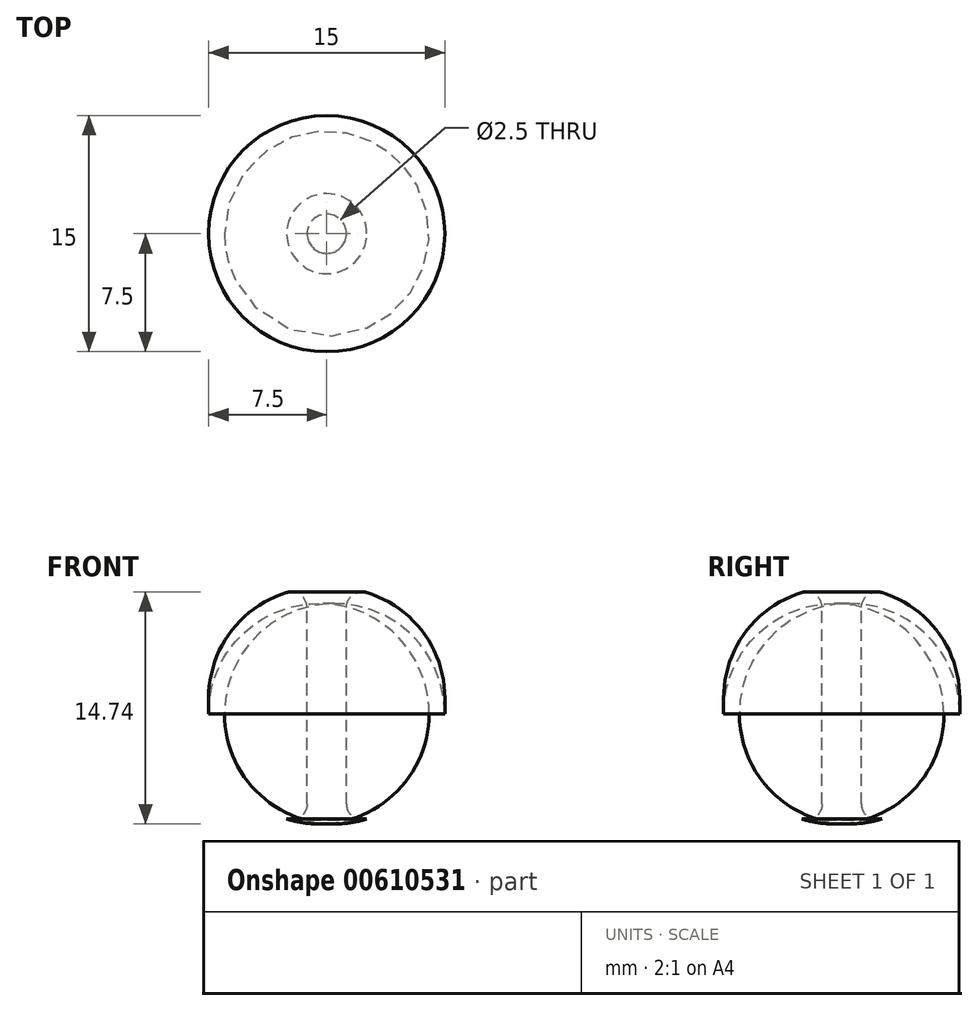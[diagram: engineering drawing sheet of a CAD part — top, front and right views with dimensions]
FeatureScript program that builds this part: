
annotation { "Feature Type Name" : "Feature", "Feature Type Description" : "" }
export const myFeature = defineFeature(function(context is Context, id is Id, definition is map)
    precondition{}
    {
        {
            var Q0;
            Q0=qCreatedBy(makeId("Top.planeOp"),FACE);
            var sketch = newSketch(context, id + "F0", { "sketchPlane" : qUnion([Q0])});
            skCircle(sketch, "E0", {"center": v(0, 0) * mm, "radius": 7.5 * mm});
            skSolve(sketch);
        }
        {
            var Q0;
            Q0=makeQuery(id+"F0.imprint","IMPRINT",FACE,{"disambiguationData":[TD([[makeQuery(id+"F0.imprint","IMPRINT",EDGE,{"derivedFrom":sQuery(id+"F0.wireOp",EDGE,"E0")}),1.0]])]});
            extrude(context, id + "F1", {"entities" : qUnion([Q0]), "depth" : 15 * mm, "offsetDistance" : 25 * mm});
        }
        {
            var Q0;
            Q0=makeQuery(id+"F1.opExtrude","CAP_EDGE",EDGE,{"disambiguationData":[OSD([sQuery(id+"F0.wireOp",EDGE,"E0")])],"isStart":false});
            fillet(context, id + "F2", {"entities" : qUnion([Q0]), "radius" : 7 * mm, "tangentPropagation" : true, "allowEdgeOverflow" : false});
        }
        {
            var Q0;
            Q0=makeQuery(id+"F1.opExtrude","CAP_EDGE",EDGE,{"disambiguationData":[OSD([sQuery(id+"F0.wireOp",EDGE,"E0")])],"isStart":true});
            fillet(context, id + "F3", {"entities" : qUnion([Q0]), "radius" : 7 * mm, "tangentPropagation" : true, "allowEdgeOverflow" : false});
        }
        {
            var Q0;
            Q0=makeQuery(id+"F1.opExtrude","CAP_FACE",FACE,{"disambiguationData":[OSD([sQuery(id+"F0.wireOp",EDGE,"E0")])],"isStart":false});
            var sketch = newSketch(context, id + "F4", { "sketchPlane" : qUnion([Q0])});
            skCircle(sketch, "E1", {"center": v(0, 0) * mm, "radius": 1.25 * mm});
            skSolve(sketch);
        }
        {
            var Q0;
            Q0=makeQuery(id+"F4.imprint","IMPRINT",FACE,{"disambiguationData":[TD([[makeQuery(id+"F4.imprint","IMPRINT",EDGE,{"derivedFrom":sQuery(id+"F4.wireOp",EDGE,"E1")}),1.0]])]});
            var Q1;
            {var subQ0=sQuery(id+"F0.wireOp",EDGE,"E0");Q1=makeQuery(id+"F4.imprint","IMPRINT",FACE,{"disambiguationData":[TD([[makeQuery(id+"F4.imprint","IMPRINT",EDGE,{"derivedFrom":makeQuery(id+"F2.opFillet","BLEND_EDGE",EDGE,{"blendedFrom":[makeQuery(id+"F1.opExtrude","CAP_EDGE",EDGE,{"disambiguationData":[OSD([subQ0])],"isStart":false}),makeQuery(id+"F1.opExtrude","CAP_FACE",FACE,{"disambiguationData":[OSD([subQ0])],"isStart":false})],"blendedInto":[makeQuery(id+"F1.opExtrude","CAP_FACE",FACE,{"disambiguationData":[OSD([subQ0])],"isStart":false})]})}),1.0]])]});}
            extrude(context, id + "F5", {"entities" : qUnion([Q0, Q1]), "operationType" : NewBodyOperationType.REMOVE, "oppositeDirection" : true, "depth" : 25 * mm, "offsetDistance" : 25 * mm});
        }
        {
            var Q0;
            Q0=makeQuery(id+"F5.boolean.opBoolean","INTERSECT",EDGE,{"derivedFrom":[makeQuery(id+"F2.opFillet","BLEND_FACE",FACE,{"disambiguationData":[OSD([sQuery(id+"F0.wireOp",EDGE,"E0")])]}),makeQuery(id+"F5.opExtrude","SWEPT_FACE",FACE,{"disambiguationData":[OSD([sQuery(id+"F4.wireOp",EDGE,"E1")])]})]});
            fillet(context, id + "F6", {"entities" : qUnion([Q0]), "radius" : 1 * mm, "tangentPropagation" : true, "allowEdgeOverflow" : false});
        }
        {
            var Q0;
            Q0=makeQuery(id+"F5.boolean.opBoolean","INTERSECT",EDGE,{"derivedFrom":[makeQuery(id+"F3.opFillet","BLEND_FACE",FACE,{"disambiguationData":[OSD([sQuery(id+"F0.wireOp",EDGE,"E0")])]}),makeQuery(id+"F5.opExtrude","SWEPT_FACE",FACE,{"disambiguationData":[OSD([sQuery(id+"F4.wireOp",EDGE,"E1")])]})]});
            fillet(context, id + "F7", {"entities" : qUnion([Q0]), "radius" : 1 * mm, "tangentPropagation" : true, "allowEdgeOverflow" : false});
        }
    });
